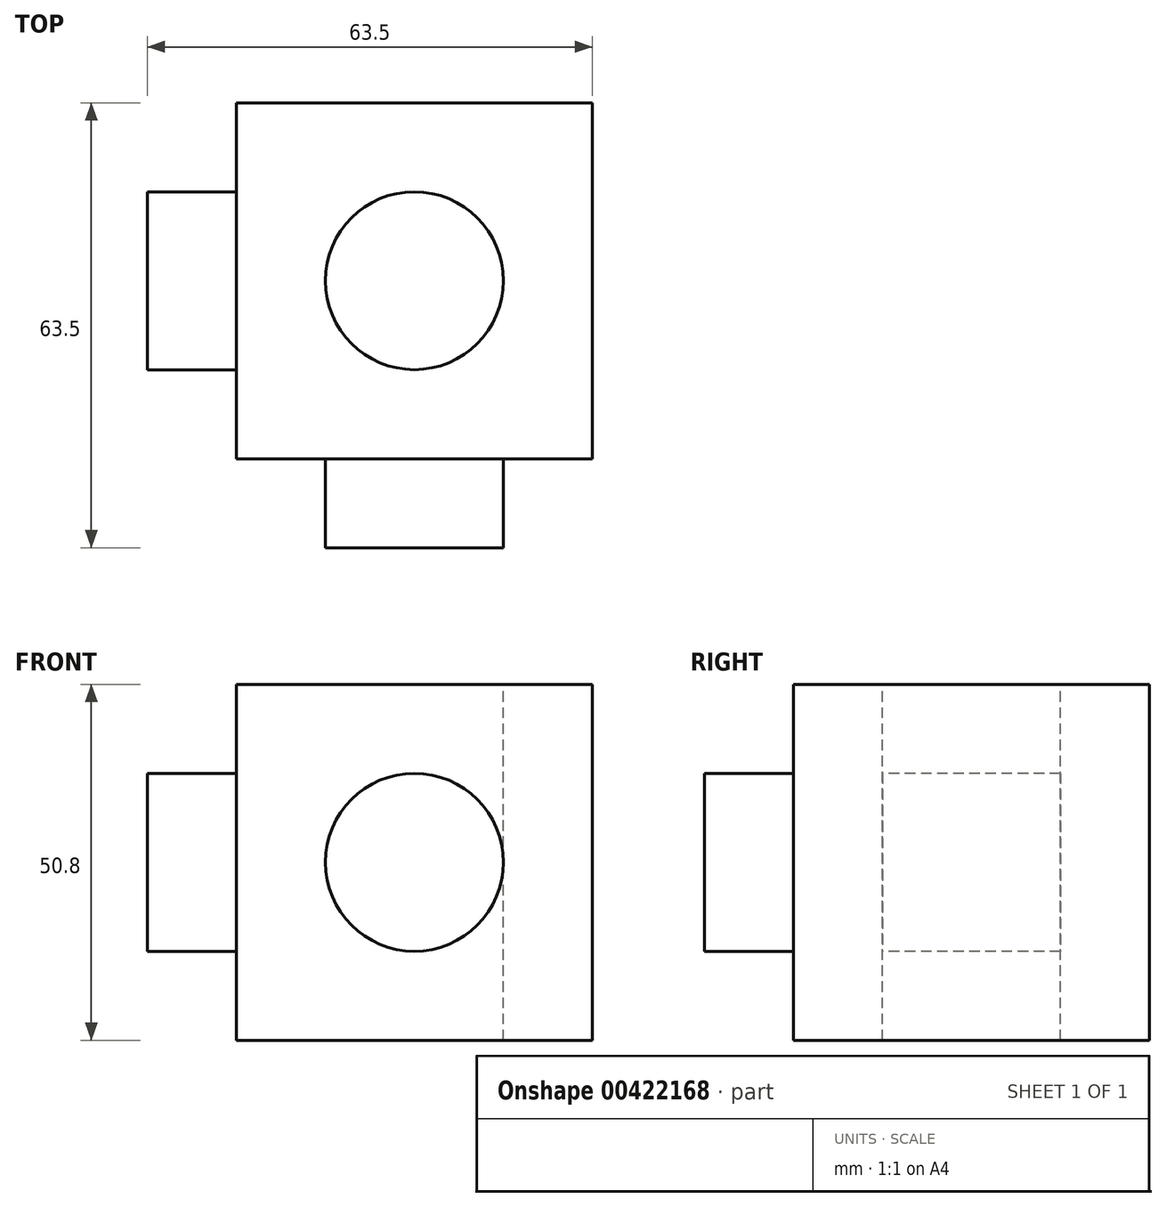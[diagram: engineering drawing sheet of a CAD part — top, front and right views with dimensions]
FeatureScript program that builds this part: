
annotation { "Feature Type Name" : "Feature", "Feature Type Description" : "" }
export const myFeature = defineFeature(function(context is Context, id is Id, definition is map)
    precondition{}
    {
        {
            var Q0;
            Q0=qCreatedBy(makeId("Front.planeOp"),FACE);
            var sketch = newSketch(context, id + "F0", { "sketchPlane" : qUnion([Q0])});
            skLineSegment(sketch, "E0", {"start": v(0, 0) * mm, "end": v(0, 50.8) * mm});
            skLineSegment(sketch, "E1", {"start": v(0, 50.8) * mm, "end": v(50.8, 50.8) * mm});
            skLineSegment(sketch, "E2", {"start": v(50.8, 50.8) * mm, "end": v(50.8, 0) * mm});
            skLineSegment(sketch, "E3", {"start": v(0, 0) * mm, "end": v(50.8, 0) * mm});
            skSolve(sketch);
        }
        {
            var Q0;
            Q0 = qSketchRegion(id + "F0", true);
            extrude(context, id + "F1", {"entities" : qUnion([Q0]), "depth" : 50.8 * mm});
        }
        {
            var Q0;
            Q0=makeQuery(id+"F1.opExtrude","CAP_FACE",FACE,{"disambiguationData":[OSD([sQuery(id+"F0.wireOp",EDGE,"E0"),sQuery(id+"F0.wireOp",EDGE,"E1"),sQuery(id+"F0.wireOp",EDGE,"E2"),sQuery(id+"F0.wireOp",EDGE,"E3")])],"isStart":false});
            var sketch = newSketch(context, id + "F2", { "sketchPlane" : qUnion([Q0])});
            skCircle(sketch, "E4", {"center": v(25.4, 25.4) * mm, "radius": 12.7 * mm});
            skSolve(sketch);
        }
        {
            var Q0;
            Q0 = qSketchRegion(id + "F2", true);
            extrude(context, id + "F3", {"entities" : qUnion([Q0]), "operationType" : NewBodyOperationType.ADD, "depth" : 12.7 * mm});
        }
        {
            var Q0;
            Q0=makeQuery(id+"F1.opExtrude","SWEPT_FACE",FACE,{"disambiguationData":[OSD([sQuery(id+"F0.wireOp",EDGE,"E1")])]});
            var sketch = newSketch(context, id + "F4", { "sketchPlane" : qUnion([Q0])});
            skCircle(sketch, "E5", {"center": v(25.4, -25.4) * mm, "radius": 12.7 * mm});
            skSolve(sketch);
        }
        {
            var Q0;
            Q0=makeQuery(id+"F4.imprint","IMPRINT",FACE,{"disambiguationData":[TD([[makeQuery(id+"F4.imprint","IMPRINT",EDGE,{"derivedFrom":sQuery(id+"F4.wireOp",EDGE,"E5")}),1.0]])]});
            extrude(context, id + "F5", {"entities" : qUnion([Q0]), "operationType" : NewBodyOperationType.REMOVE, "oppositeDirection" : true, "depth" : 50.8 * mm});
        }
        {
            var Q0;
            Q0=makeQuery(id+"F1.opExtrude","SWEPT_FACE",FACE,{"disambiguationData":[OSD([sQuery(id+"F0.wireOp",EDGE,"E0")])]});
            var sketch = newSketch(context, id + "F6", { "sketchPlane" : qUnion([Q0])});
            skLineSegment(sketch, "E6.bottom", {"start": v(12.7, 38.1) * mm, "end": v(38.1, 38.1) * mm});
            skLineSegment(sketch, "E6.top", {"start": v(12.7, 12.7) * mm, "end": v(38.1, 12.7) * mm});
            skLineSegment(sketch, "E6.left", {"start": v(12.7, 38.1) * mm, "end": v(12.7, 12.7) * mm});
            skLineSegment(sketch, "E6.right", {"start": v(38.1, 38.1) * mm, "end": v(38.1, 12.7) * mm});
            skSolve(sketch);
        }
        {
            var Q0;
            Q0 = qSketchRegion(id + "F6", true);
            extrude(context, id + "F7", {"entities" : qUnion([Q0]), "operationType" : NewBodyOperationType.ADD, "depth" : 12.7 * mm});
        }
    });
